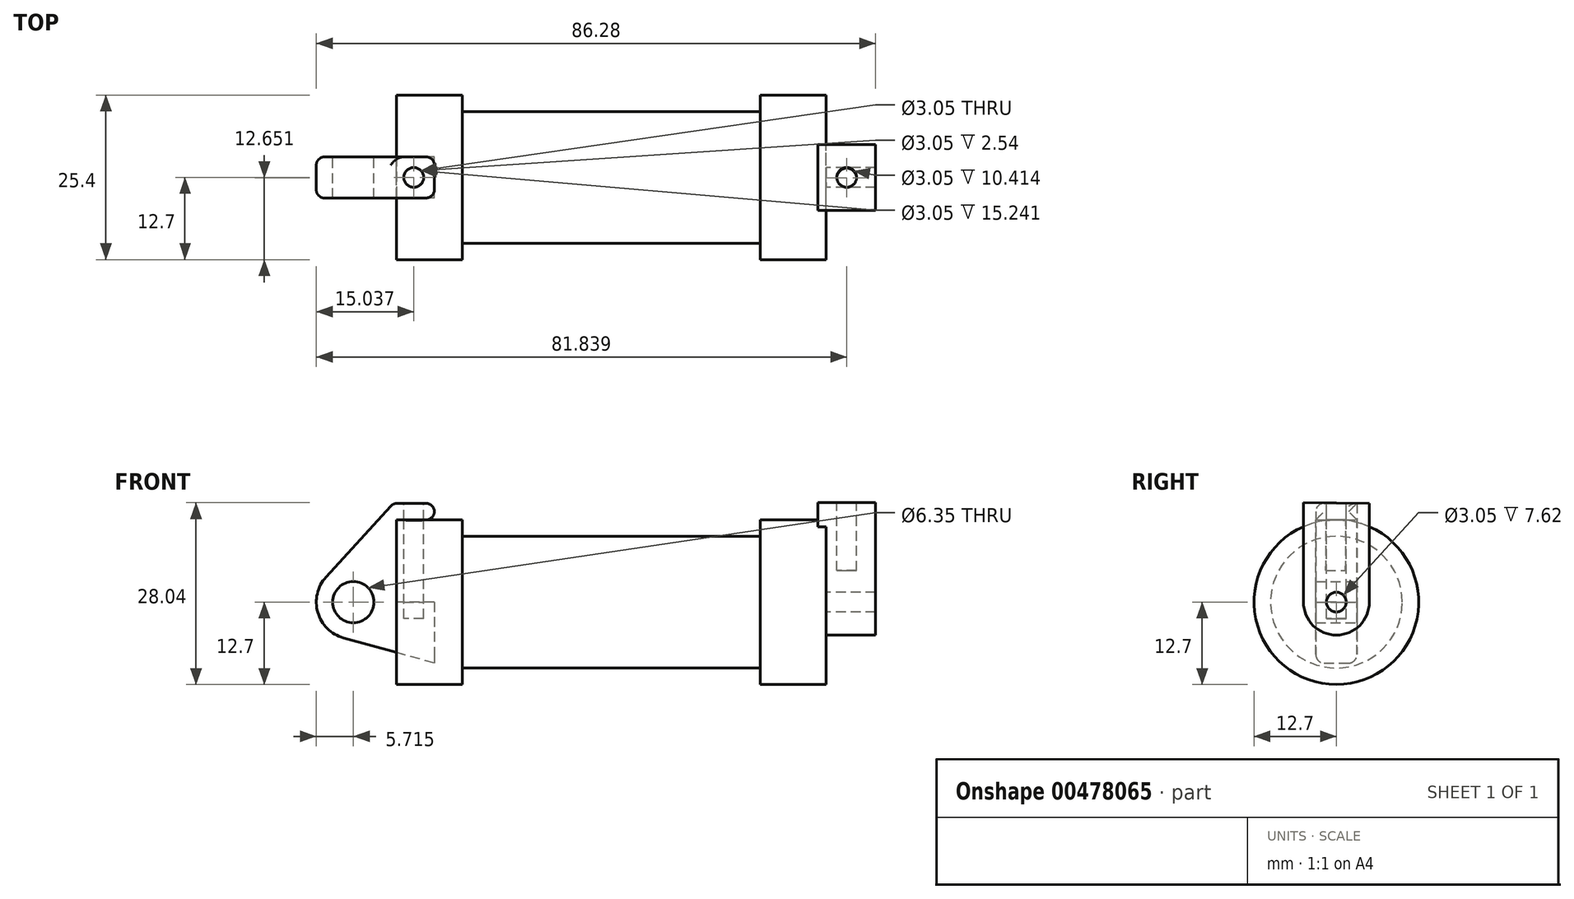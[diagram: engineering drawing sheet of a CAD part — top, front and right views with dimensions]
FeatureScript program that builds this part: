
annotation { "Feature Type Name" : "Feature", "Feature Type Description" : "" }
export const myFeature = defineFeature(function(context is Context, id is Id, definition is map)
    precondition{}
    {
        {
            var Q0;
            Q0=qCreatedBy(makeId("Front.planeOp"),FACE);
            var sketch = newSketch(context, id + "F0", { "sketchPlane" : qUnion([Q0])});
            skLineSegment(sketch, "E0", {"start": v(0, 0) * mm, "end": v(0, 12.7) * mm});
            skLineSegment(sketch, "E1", {"start": v(0, 12.7) * mm, "end": v(10.16, 12.7) * mm});
            skLineSegment(sketch, "E2", {"start": v(10.16, 12.7) * mm, "end": v(10.16, 10.16) * mm});
            skLineSegment(sketch, "E3", {"start": v(10.16, 10.16) * mm, "end": v(56.13, 10.16) * mm});
            skLineSegment(sketch, "E4", {"start": v(56.13, 10.16) * mm, "end": v(56.13, 12.7) * mm});
            skLineSegment(sketch, "E5", {"start": v(56.13, 12.7) * mm, "end": v(66.3, 12.7) * mm});
            skLineSegment(sketch, "E6", {"start": v(66.3, 12.7) * mm, "end": v(66.3, 0) * mm});
            skLineSegment(sketch, "E7", {"start": v(66.3, 0) * mm, "end": v(0, 0) * mm});
            skLineSegment(sketch, "E8", {"start": v(5.84, 15.24) * mm, "end": v(-0.5, 15.24) * mm});
            skLineSegment(sketch, "E9", {"start": v(-0.5, 15.24) * mm, "end": v(-10.88, 3.85) * mm});
            skLineSegment(sketch, "E10", {"start": v(0, 0) * mm, "end": v(-6.65, 0) * mm});
            skCircle(sketch, "E11", {"center": v(-6.65, 0) * mm, "radius": 5.72 * mm});
            skCircle(sketch, "E12", {"center": v(-6.65, 0) * mm, "radius": 3.18 * mm});
            skLineSegment(sketch, "E13", {"start": v(5.84, 15.24) * mm, "end": v(5.84, -9.4) * mm});
            skLineSegment(sketch, "E14", {"start": v(5.84, -9.4) * mm, "end": v(-8.18, -5.5) * mm});
            skSolve(sketch);
        }
        {
            var Q0;
            {var subQ0=sQuery(id+"F0.wireOp",EDGE,"E0");Q0=makeQuery(id+"F0.imprint","IMPRINT",FACE,{"disambiguationData":[TD([[makeQuery(id+"F0.imprint","IMPRINT",EDGE,{"derivedFrom":subQ0}),-1.0]])]});}
            var Q1;
            {var subQ0=sQuery(id+"F0.wireOp",EDGE,"E2");Q1=makeQuery(id+"F0.imprint","IMPRINT",FACE,{"disambiguationData":[TD([[makeQuery(id+"F0.imprint","IMPRINT",EDGE,{"derivedFrom":subQ0}),-1.0]])]});}
            var Q2;
            Q2=sQuery(id+"F0.wireOp",EDGE,"E7");
            revolve(context, id + "F1", {"entities" : qUnion([Q0, Q1]), "axis" : qUnion([Q2]), "revolveType" : RevolveType.FULL});
        }
        {
            var Q0;
            {var subQ1=sQuery(id+"F0.wireOp",EDGE,"E0");Q0=makeQuery(id+"F0.imprint","IMPRINT",FACE,{"disambiguationData":[TD([[makeQuery(id+"F0.imprint","IMPRINT",EDGE,{"derivedFrom":subQ1}),1.0]])]});}
            var Q1;
            {var subQ5=sQuery(id+"F0.wireOp",EDGE,"E12");Q1=makeQuery(id+"F0.imprint","IMPRINT",FACE,{"disambiguationData":[TD([[makeQuery(id+"F0.imprint","IMPRINT",EDGE,{"derivedFrom":subQ5}),-1.0]])]});}
            var Q2;
            {var subQ0=sQuery(id+"F0.wireOp",EDGE,"E14");Q2=makeQuery(id+"F0.imprint","IMPRINT",FACE,{"disambiguationData":[TD([[makeQuery(id+"F0.imprint","IMPRINT",EDGE,{"derivedFrom":subQ0}),-1.0]])]});}
            var Q3;
            Q3=sQuery(id+"F0.wireOp",EDGE,"E9");
            var Q4;
            Q4=sQuery(id+"F0.wireOp",EDGE,"E11");
            var Q5;
            Q5=sQuery(id+"F0.wireOp",EDGE,"E12");
            var Q6;
            Q6=sQuery(id+"F0.wireOp",EDGE,"E14");
            var Q7;
            Q7=sQuery(id+"F0.wireOp",EDGE,"E8");
            extrude(context, id + "F2", {"entities" : qUnion([Q0, Q1, Q2]), "surfaceEntities" : qUnion([Q3, Q4, Q5, Q6, Q7]), "endBound" : BoundingType.SYMMETRIC, "depth" : 6.35 * mm});
        }
        {
            var Q0;
            Q0=makeQuery(id+"F1.opRevolve","SWEPT_FACE",FACE,{"disambiguationData":[OSD([sQuery(id+"F0.wireOp",EDGE,"E6")])]});
            var sketch = newSketch(context, id + "F3", { "sketchPlane" : qUnion([Q0])});
            skCircle(sketch, "E15", {"center": v(0, 0) * mm, "radius": 5.08 * mm});
            skCircle(sketch, "E16", {"center": v(0, 0) * mm, "radius": 1.52 * mm});
            skLineSegment(sketch, "E17", {"start": v(-5.08, 0) * mm, "end": v(-5.08, 15.34) * mm});
            skLineSegment(sketch, "E18", {"start": v(5.08, 0) * mm, "end": v(5.08, 15.24) * mm});
            skLineSegment(sketch, "E19", {"start": v(5.08, 15.24) * mm, "end": v(-5.08, 15.34) * mm});
            skSolve(sketch);
        }
        {
            var Q0;
            Q0 = qSketchRegion(id + "F3", true);
            extrude(context, id + "F4", {"entities" : qUnion([Q0]), "operationType" : NewBodyOperationType.ADD, "depth" : 7.62 * mm});
        }
        {
            var Q0;
            {var subQ0=sQuery(id+"F3.wireOp",EDGE,"E19");Q0=makeQuery(id+"F3.imprint","IMPRINT",FACE,{"disambiguationData":[TD([[makeQuery(id+"F3.imprint","IMPRINT",EDGE,{"derivedFrom":subQ0}),1.0]])]});}
            extrude(context, id + "F5", {"entities" : qUnion([Q0]), "operationType" : NewBodyOperationType.ADD, "oppositeDirection" : true, "depth" : 1.27 * mm});
        }
        {
            var Q0;
            {var subQ0=sQuery(id+"F3.wireOp",EDGE,"E19");Q0=makeQuery(id+"F5.boolean.opBoolean","MERGE",FACE,{"derivedFrom":[makeQuery(id+"F4.opExtrude","SWEPT_FACE",FACE,{"disambiguationData":[OSD([subQ0])]}),makeQuery(id+"F5.opExtrude","SWEPT_FACE",FACE,{"disambiguationData":[OSD([subQ0])]})]});}
            var sketch = newSketch(context, id + "F6", { "sketchPlane" : qUnion([Q0])});
            skLineSegment(sketch, "E20", {"start": v(73.91, -5.22) * mm, "end": v(65.02, -5.22) * mm});
            skCircle(sketch, "E21", {"center": v(69.47, -0.14) * mm, "radius": 1.52 * mm});
            skCircle(sketch, "E22", {"center": v(2.65, -0.18) * mm, "radius": 1.52 * mm});
            skSolve(sketch);
        }
        {
            var Q0;
            Q0=makeQuery(id+"F6.imprint","IMPRINT",FACE,{"disambiguationData":[TD([[makeQuery(id+"F6.imprint","IMPRINT",EDGE,{"derivedFrom":sQuery(id+"F6.wireOp",EDGE,"E21")}),1.0]])]});
            var Q1;
            Q1=sQuery(id+"F6.wireOp",EDGE,"E21");
            extrude(context, id + "F7", {"entities" : qUnion([Q0]), "operationType" : NewBodyOperationType.REMOVE, "surfaceEntities" : qUnion([Q1]), "oppositeDirection" : true, "depth" : 10.4 * mm});
        }
        {
            var Q0;
            Q0=makeQuery(id+"F2.opExtrude","SWEPT_FACE",FACE,{"disambiguationData":[OSD([sQuery(id+"F0.wireOp",EDGE,"E8")])]});
            var sketch = newSketch(context, id + "F8", { "sketchPlane" : qUnion([Q0])});
            skCircle(sketch, "E23", {"center": v(2.67, 0) * mm, "radius": 1.52 * mm});
            skSolve(sketch);
        }
        {
            var Q0;
            Q0=makeQuery(id+"F8.imprint","IMPRINT",FACE,{"disambiguationData":[TD([[makeQuery(id+"F8.imprint","IMPRINT",EDGE,{"derivedFrom":sQuery(id+"F8.wireOp",EDGE,"E23")}),1.0]])]});
            var Q1;
            Q1=sQuery(id+"F8.wireOp",EDGE,"E23");
            extrude(context, id + "F9", {"entities" : qUnion([Q0]), "operationType" : NewBodyOperationType.REMOVE, "surfaceEntities" : qUnion([Q1]), "oppositeDirection" : true, "depth" : 17.78 * mm});
        }
        {
            var Q0;
            Q0=makeQuery(id+"F2.opExtrude","CAP_EDGE",EDGE,{"disambiguationData":[OSD([sQuery(id+"F0.wireOp",EDGE,"E8")])],"isStart":false});
            var Q1;
            Q1=makeQuery(id+"F1.opRevolve","SWEPT_EDGE",EDGE,{"disambiguationData":[OSD([sQuery(id+"F0.wireOp",EDGE,"E1"),sQuery(id+"F0.wireOp",EDGE,"E2")])]});
            var Q2;
            Q2=makeQuery(id+"F1.opRevolve","SWEPT_EDGE",EDGE,{"disambiguationData":[OSD([sQuery(id+"F0.wireOp",EDGE,"E4"),sQuery(id+"F0.wireOp",EDGE,"E5")])]});
            var Q3;
            Q3=makeQuery(id+"F5.opExtrude","CAP_EDGE",EDGE,{"disambiguationData":[OSD([sQuery(id+"F3.wireOp",EDGE,"E18")])],"isStart":false});
            var Q4;
            Q4=makeQuery(id+"F2.opExtrude","SWEPT_FACE",FACE,{"disambiguationData":[OSD([sQuery(id+"F0.wireOp",EDGE,"E9")])]});
            var Q5;
            Q5=makeQuery(id+"F2.opExtrude","SWEPT_FACE",FACE,{"disambiguationData":[OSD([sQuery(id+"F0.wireOp",EDGE,"E11")])]});
            var Q6;
            Q6=makeQuery(id+"F1.opRevolve","SWEPT_FACE",FACE,{"disambiguationData":[OSD([sQuery(id+"F0.wireOp",EDGE,"E1")])]});
            var Q7;
            Q7=makeQuery(id+"F7.boolean.opBoolean","COPY",FACE,{"derivedFrom":makeQuery(id+"F7.opExtrude","CAP_FACE",FACE,{"disambiguationData":[OSD([sQuery(id+"F6.wireOp",EDGE,"E21")])],"isStart":false})});
            var Q8;
            Q8=makeQuery(id+"F5.opExtrude","CAP_FACE",FACE,{"disambiguationData":[OSD([sQuery(id+"F0.wireOp",EDGE,"E5"),sQuery(id+"F0.wireOp",EDGE,"E6"),sQuery(id+"F3.wireOp",EDGE,"E17"),sQuery(id+"F3.wireOp",EDGE,"E18"),sQuery(id+"F3.wireOp",EDGE,"E19")])],"isStart":false});
            var Q9;
            {var subQ0=sQuery(id+"F3.wireOp",EDGE,"E19");var subQ1=sQuery(id+"F3.wireOp",EDGE,"E17");Q9=makeQuery(id+"F5.boolean.opBoolean","MERGE",EDGE,{"derivedFrom":[makeQuery(id+"F4.opExtrude","SWEPT_EDGE",EDGE,{"disambiguationData":[OSD([subQ1,subQ0])]}),makeQuery(id+"F5.opExtrude","SWEPT_EDGE",EDGE,{"disambiguationData":[OSD([subQ1,subQ0])]})]});}
            var Q10;
            {var subQ0=sQuery(id+"F3.wireOp",EDGE,"E19");var subQ1=sQuery(id+"F3.wireOp",EDGE,"E18");Q10=makeQuery(id+"F5.boolean.opBoolean","MERGE",EDGE,{"derivedFrom":[makeQuery(id+"F4.opExtrude","SWEPT_EDGE",EDGE,{"disambiguationData":[OSD([subQ1,subQ0])]}),makeQuery(id+"F5.opExtrude","SWEPT_EDGE",EDGE,{"disambiguationData":[OSD([subQ1,subQ0])]})]});}
            var Q11;
            Q11=makeQuery(id+"F4.opExtrude","CAP_EDGE",EDGE,{"disambiguationData":[OSD([sQuery(id+"F3.wireOp",EDGE,"E19")])],"isStart":false});
            var Q12;
            {var subQ0=sQuery(id+"F0.wireOp",EDGE,"E13");Q12=makeQuery(id+"F2.opExtrude","SWEPT_FACE",FACE,{"disambiguationData":[OSD([subQ0]),TDD([makeQuery(id+"F0.imprint","IMPRINT",EDGE,{"disambiguationData":[TD([[makeQuery(id+"F0.imprint","INTERSECT",VERTEX,{"derivedFrom":[sQuery(id+"F0.wireOp",EDGE,"E8"),subQ0]}),-1.0]])],"derivedFrom":subQ0})])]});}
            var Q13;
            Q13=makeQuery(id+"F2.opExtrude","CAP_EDGE",EDGE,{"disambiguationData":[OSD([sQuery(id+"F0.wireOp",EDGE,"E11")])],"isStart":true});
            var Q14;
            Q14=makeQuery(id+"F4.opExtrude","CAP_EDGE",EDGE,{"disambiguationData":[OSD([sQuery(id+"F3.wireOp",EDGE,"E15")])],"isStart":false});
            var Q15;
            {var subQ0=sQuery(id+"F0.wireOp",EDGE,"E5");var subQ1=sQuery(id+"F0.wireOp",EDGE,"E6");Q15=makeQuery(id+"F4.boolean.opBoolean","SPLIT",EDGE,{"disambiguationData":[topologyDisambiguationEdgeConnected([makeQuery(id+"F1.opRevolve","SWEPT_FACE",FACE,{"disambiguationData":[OSD([subQ1])]})])],"derivedFrom":makeQuery(id+"F1.opRevolve","SWEPT_EDGE",EDGE,{"disambiguationData":[OSD([subQ0,subQ1])]})});}
            var Q16;
            Q16=makeQuery(id+"F1.opRevolve","SWEPT_EDGE",EDGE,{"disambiguationData":[OSD([sQuery(id+"F0.wireOp",EDGE,"E2"),sQuery(id+"F0.wireOp",EDGE,"E3")])]});
            var Q17;
            Q17=makeQuery(id+"F1.opRevolve","SWEPT_EDGE",EDGE,{"disambiguationData":[OSD([sQuery(id+"F0.wireOp",EDGE,"E3"),sQuery(id+"F0.wireOp",EDGE,"E4")])]});
            fillet(context, id + "F10", {"entities" : qUnion([Q0, Q1, Q2, Q3, Q4, Q5, Q6, Q7, Q8, Q9, Q10, Q11, Q12, Q13, Q14, Q15, Q16, Q17]), "radius" : 1.27 * mm, "tangentPropagation" : true, "allowEdgeOverflow" : false});
        }
    });
